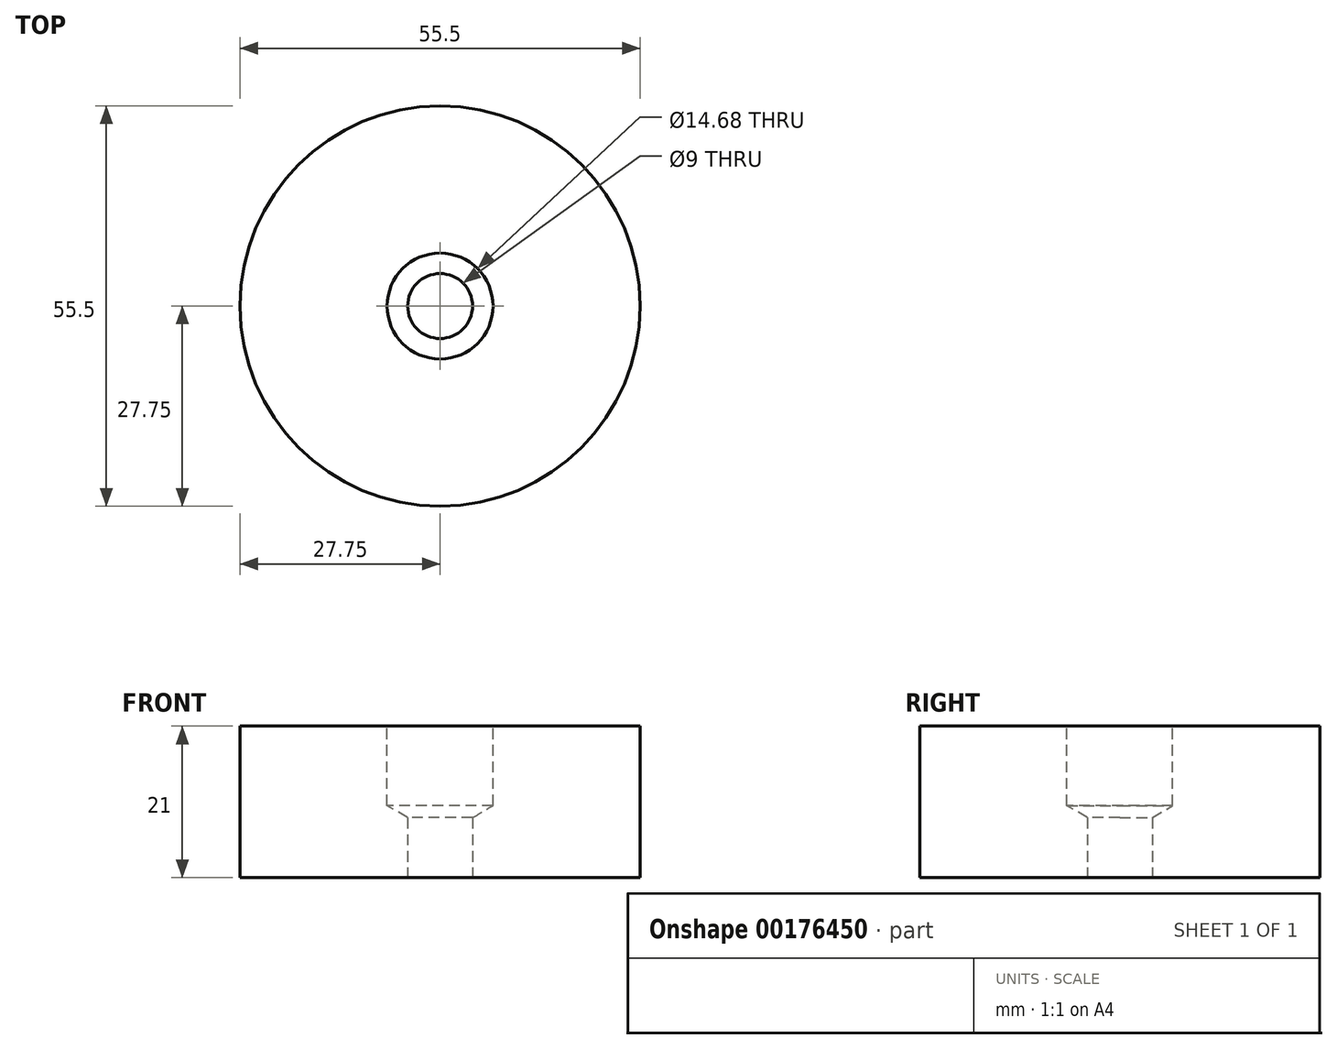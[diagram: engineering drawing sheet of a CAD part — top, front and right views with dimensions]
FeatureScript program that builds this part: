
annotation { "Feature Type Name" : "Feature", "Feature Type Description" : "" }
export const myFeature = defineFeature(function(context is Context, id is Id, definition is map)
    precondition{}
    {
        {
            var Q0;
            Q0=qCreatedBy(makeId("Top.planeOp"),FACE);
            var sketch = newSketch(context, id + "F0", { "sketchPlane" : qUnion([Q0])});
            skCircle(sketch, "E0", {"center": v(0, 0) * mm, "radius": 27.75 * mm});
            skSolve(sketch);
        }
        {
            var Q0;
            Q0=makeQuery(id+"F0.imprint","IMPRINT",FACE,{"disambiguationData":[TD([[makeQuery(id+"F0.imprint","IMPRINT",EDGE,{"derivedFrom":sQuery(id+"F0.wireOp",EDGE,"E0")}),1.0]])]});
            extrude(context, id + "F1", {"entities" : qUnion([Q0]), "depth" : 21 * mm});
        }
        {
            var Q0;
            Q0=makeQuery(id+"F1.opExtrude","CAP_FACE",FACE,{"disambiguationData":[OSD([sQuery(id+"F0.wireOp",EDGE,"E0")])],"isStart":false});
            var sketch = newSketch(context, id + "F2", { "sketchPlane" : qUnion([Q0])});
            skCircle(sketch, "E1", {"center": v(0, 0) * mm, "radius": 6 * mm});
            skSolve(sketch);
        }
        {
            var Q0;
            Q0=sQuery(id+"F2.wireOp",VERTEX,"E1.center");
            var Q1;
            Q1=makeQuery(id+"F1.opExtrude","SWEPT_BODY",BODY,{"disambiguationData":[OSD([sQuery(id+"F0.wireOp",EDGE,"E0")])]});
            hole(context, id + "F3", {"style" : HoleStyle.SIMPLE, "endStyle" : HoleEndStyle.BLIND, "standardTappedOrClearance" : lookupTablePath({ "standard" : "ANSI", "engagement" : "75%", "pitch" : "24 tpi", "size" : "5/8", "type" : "Tapped" }), "standardBlindInLast" : lookupTablePath({ "standard" : "ANSI", "engagement" : "75%", "pitch" : "24 tpi", "size" : "5/8", "type" : "Tapped" }), "holeDiameter" : 14.68 * mm, "holeDepth" : 11 * mm, "startFromSketch" : true, "locations" : qUnion([Q0]), "scope" : qUnion([Q1]), "majorDiameter" : 15.88 * mm});
        }
        {
            var Q0;
            Q0=makeQuery(id+"F1.opExtrude","CAP_FACE",FACE,{"disambiguationData":[OSD([sQuery(id+"F0.wireOp",EDGE,"E0")])],"isStart":true});
            var sketch = newSketch(context, id + "F4", { "sketchPlane" : qUnion([Q0])});
            skCircle(sketch, "E2", {"center": v(0, 0) * mm, "radius": 4.57 * mm});
            skSolve(sketch);
        }
        {
            var Q0;
            Q0=sQuery(id+"F4.wireOp",VERTEX,"E2.center");
            var Q1;
            Q1=makeQuery(id+"F1.opExtrude","SWEPT_BODY",BODY,{"disambiguationData":[OSD([sQuery(id+"F0.wireOp",EDGE,"E0")])]});
            hole(context, id + "F5", {"style" : HoleStyle.SIMPLE, "endStyle" : HoleEndStyle.BLIND, "holeDiameter" : 9 * mm, "holeDepth" : 13.75 * mm, "startFromSketch" : true, "locations" : qUnion([Q0]), "scope" : qUnion([Q1])});
        }
    });
